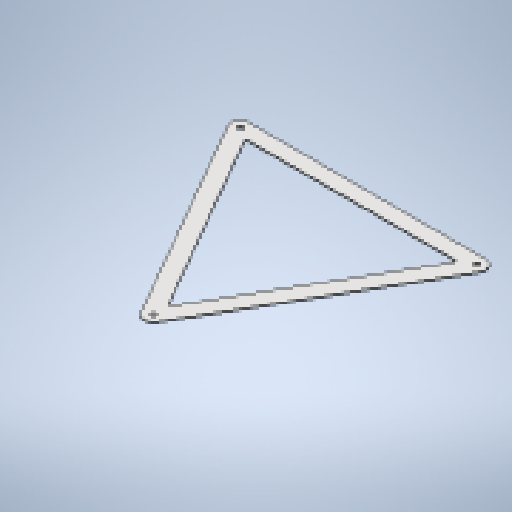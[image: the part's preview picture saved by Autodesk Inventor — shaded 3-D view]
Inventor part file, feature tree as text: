
AUTODESK INVENTOR PART (.ipt)
format: ipt  version: 2025.1 (Build 291241020, 241B)  size: 195,072 bytes
history: native  units: mm
features: other x2, sheet_metal_op x1, chamfer x1, sketch x1
ambient origin geometry x8: Origin, YZ Plane, XZ Plane, XY Plane, X Axis, Y Axis, Z Axis, Center Point
bodies: Solid1 (feature_tree)
feature tree (5):
  sheet_metal_op  "Face1"
  chamfer  "Corner Round3"
  sketch  "Sketch1"  dims[d2=3.0mm d34=17.0mm d35=20.0mm d36=740.47mm d37=740.47mm d38=50.0mm d39=6.0mm]
  other  "Plate1"
  other  "Definition1"
